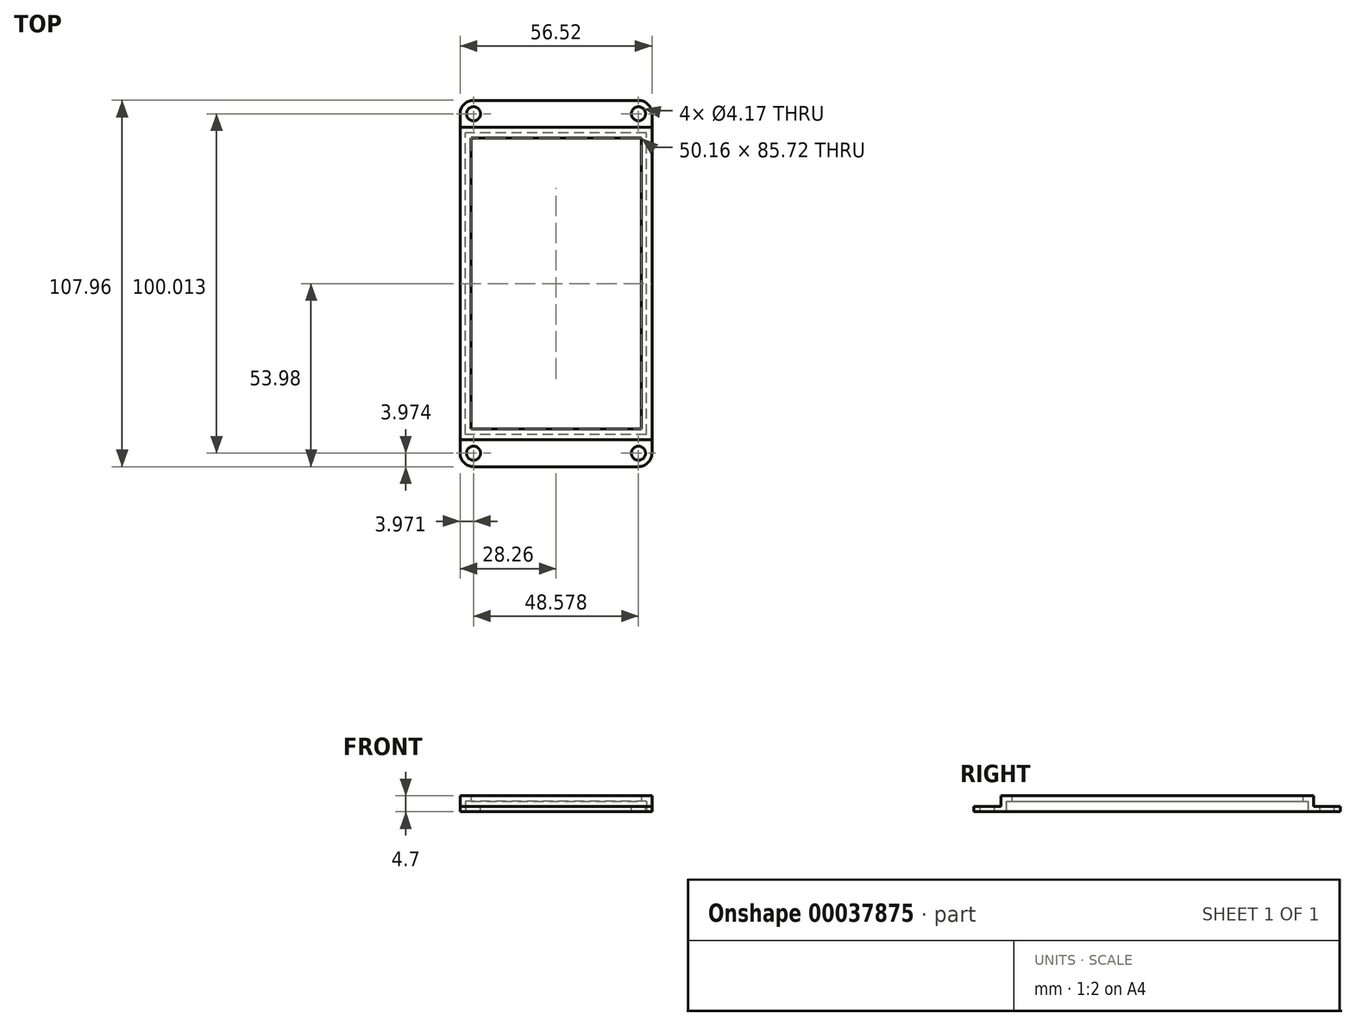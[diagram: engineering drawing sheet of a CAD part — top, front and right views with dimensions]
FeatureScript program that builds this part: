
annotation { "Feature Type Name" : "Feature", "Feature Type Description" : "" }
export const myFeature = defineFeature(function(context is Context, id is Id, definition is map)
    precondition{}
    {
        {
            var Q0;
            Q0=qCreatedBy(makeId("Top.planeOp"),FACE);
            var sketch = newSketch(context, id + "F0", { "sketchPlane" : qUnion([Q0])});
            skLineSegment(sketch, "E0.rect.bottom", {"start": v(26.67, -44.45) * mm, "end": v(-26.67, -44.45) * mm});
            skLineSegment(sketch, "E0.rect.top", {"start": v(26.67, 44.45) * mm, "end": v(-26.67, 44.45) * mm});
            skLineSegment(sketch, "E0.rect.left", {"start": v(26.67, -44.45) * mm, "end": v(26.67, 44.45) * mm});
            skLineSegment(sketch, "E0.rect.right", {"start": v(-26.67, -44.45) * mm, "end": v(-26.67, 44.45) * mm});
            skPoint(sketch, "E0.rect.middle", {"position": v(0, 0) * mm});
            skLineSegment(sketch, "E1.rect.bottom", {"start": v(28.26, -46.04) * mm, "end": v(-28.26, -46.04) * mm});
            skLineSegment(sketch, "E1.rect.top", {"start": v(28.26, 46.04) * mm, "end": v(-28.26, 46.04) * mm});
            skLineSegment(sketch, "E1.rect.left", {"start": v(28.26, -46.04) * mm, "end": v(28.26, 46.04) * mm});
            skLineSegment(sketch, "E1.rect.right", {"start": v(-28.26, -46.04) * mm, "end": v(-28.26, 46.04) * mm});
            skLineSegment(sketch, "E2.bottom", {"start": v(26.67, -44.45) * mm, "end": v(28.26, -44.45) * mm, "construction": true});
            skLineSegment(sketch, "E2.left", {"start": v(26.67, -44.45) * mm, "end": v(26.67, -46.04) * mm, "construction": true});
            skSolve(sketch);
        }
        {
            var Q0;
            Q0 = qSketchRegion(id + "F0", true);
            extrude(context, id + "F1", {"entities" : qUnion([Q0]), "depth" : 1.52 * mm});
        }
        {
            var Q0;
            Q0=makeQuery(id+"F1.opExtrude","CAP_FACE",FACE,{"disambiguationData":[OSD([sQuery(id+"F0.wireOp",EDGE,"E0.rect.bottom"),sQuery(id+"F0.wireOp",EDGE,"E0.rect.top"),sQuery(id+"F0.wireOp",EDGE,"E0.rect.left"),sQuery(id+"F0.wireOp",EDGE,"E0.rect.right"),sQuery(id+"F0.wireOp",EDGE,"E1.rect.bottom"),sQuery(id+"F0.wireOp",EDGE,"E1.rect.top"),sQuery(id+"F0.wireOp",EDGE,"E1.rect.left"),sQuery(id+"F0.wireOp",EDGE,"E1.rect.right")])],"isStart":true});
            var sketch = newSketch(context, id + "F2", { "sketchPlane" : qUnion([Q0])});
            skLineSegment(sketch, "E3", {"start": v(-26.67, 0) * mm, "end": v(26.67, 0) * mm, "construction": true});
            skPoint(sketch, "E3.endSnap0", {"position": v(-26.67, 0) * mm});
            skLineSegment(sketch, "E4.rect.bottom", {"start": v(-28.26, 53.98) * mm, "end": v(28.26, 53.98) * mm});
            skLineSegment(sketch, "E4.rect.top", {"start": v(-28.26, -53.97) * mm, "end": v(28.26, -53.97) * mm});
            skLineSegment(sketch, "E4.rect.left", {"start": v(-28.26, 53.98) * mm, "end": v(-28.26, -53.98) * mm});
            skLineSegment(sketch, "E4.rect.right", {"start": v(28.26, 53.98) * mm, "end": v(28.26, -53.98) * mm});
            skPoint(sketch, "E4.rect.middle", {"position": v(0, 0) * mm});
            skLineSegment(sketch, "E5", {"start": v(0, 53.98) * mm, "end": v(0, 50) * mm, "construction": true});
            skLineSegment(sketch, "E6", {"start": v(0, 50) * mm, "end": v(0, 46.04) * mm, "construction": true});
            skLineSegment(sketch, "E7", {"start": v(-24.29, 50) * mm, "end": v(24.29, 50) * mm, "construction": true});
            skLineSegment(sketch, "E8", {"start": v(24.29, 50) * mm, "end": v(28.26, 50) * mm, "construction": true});
            skLineSegment(sketch, "E9", {"start": v(0, -53.97) * mm, "end": v(0, -50) * mm, "construction": true});
            skLineSegment(sketch, "E10", {"start": v(-24.29, -50) * mm, "end": v(24.29, -50) * mm, "construction": true});
            skLineSegment(sketch, "E11.rect.bottom", {"start": v(-26.67, 44.45) * mm, "end": v(26.67, 44.45) * mm});
            skLineSegment(sketch, "E11.rect.top", {"start": v(-26.67, -44.45) * mm, "end": v(26.67, -44.45) * mm});
            skLineSegment(sketch, "E11.rect.left", {"start": v(-26.67, 44.45) * mm, "end": v(-26.67, -44.45) * mm});
            skLineSegment(sketch, "E11.rect.right", {"start": v(26.67, 44.45) * mm, "end": v(26.67, -44.45) * mm});
            skCircle(sketch, "E12", {"center": v(-24.29, 50) * mm, "radius": 2.08 * mm});
            skCircle(sketch, "E13", {"center": v(24.29, 50) * mm, "radius": 2.08 * mm});
            skCircle(sketch, "E14", {"center": v(24.29, -50) * mm, "radius": 2.08 * mm});
            skCircle(sketch, "E15", {"center": v(-24.29, -50) * mm, "radius": 2.08 * mm});
            skSolve(sketch);
        }
        {
            var Q0;
            Q0 = qSketchRegion(id + "F2", true);
            extrude(context, id + "F3", {"entities" : qUnion([Q0]), "operationType" : NewBodyOperationType.ADD, "depth" : 1.59 * mm});
        }
        {
            var Q0;
            Q0=makeQuery(id+"F1.opExtrude","CAP_FACE",FACE,{"disambiguationData":[OSD([sQuery(id+"F0.wireOp",EDGE,"E0.rect.bottom"),sQuery(id+"F0.wireOp",EDGE,"E0.rect.top"),sQuery(id+"F0.wireOp",EDGE,"E0.rect.left"),sQuery(id+"F0.wireOp",EDGE,"E0.rect.right"),sQuery(id+"F0.wireOp",EDGE,"E1.rect.bottom"),sQuery(id+"F0.wireOp",EDGE,"E1.rect.top"),sQuery(id+"F0.wireOp",EDGE,"E1.rect.left"),sQuery(id+"F0.wireOp",EDGE,"E1.rect.right")])],"isStart":false});
            var sketch = newSketch(context, id + "F4", { "sketchPlane" : qUnion([Q0])});
            skLineSegment(sketch, "E16", {"start": v(-26.67, 0) * mm, "end": v(26.67, 0) * mm, "construction": true});
            skLineSegment(sketch, "E17.rect.bottom", {"start": v(-28.26, -46.04) * mm, "end": v(28.26, -46.04) * mm});
            skLineSegment(sketch, "E17.rect.top", {"start": v(-28.26, 46.04) * mm, "end": v(28.26, 46.04) * mm});
            skLineSegment(sketch, "E17.rect.left", {"start": v(-28.26, -46.04) * mm, "end": v(-28.26, 46.04) * mm});
            skLineSegment(sketch, "E17.rect.right", {"start": v(28.26, -46.04) * mm, "end": v(28.26, 46.04) * mm});
            skPoint(sketch, "E17.rect.middle", {"position": v(0, 0) * mm});
            skLineSegment(sketch, "E18.rect.bottom", {"start": v(-25.08, -42.86) * mm, "end": v(25.08, -42.86) * mm});
            skLineSegment(sketch, "E18.rect.top", {"start": v(-25.08, 42.86) * mm, "end": v(25.08, 42.86) * mm});
            skLineSegment(sketch, "E18.rect.left", {"start": v(-25.08, -42.86) * mm, "end": v(-25.08, 42.86) * mm});
            skLineSegment(sketch, "E18.rect.right", {"start": v(25.08, -42.86) * mm, "end": v(25.08, 42.86) * mm});
            skSolve(sketch);
        }
        {
            var Q0;
            Q0 = qSketchRegion(id + "F4", true);
            extrude(context, id + "F5", {"entities" : qUnion([Q0]), "operationType" : NewBodyOperationType.ADD, "depth" : 1.59 * mm});
        }
        {
            var Q0;
            Q0=makeQuery(id+"F3.opExtrude","SWEPT_EDGE",EDGE,{"disambiguationData":[OSD([sQuery(id+"F2.wireOp",EDGE,"E4.rect.bottom"),sQuery(id+"F2.wireOp",EDGE,"E4.rect.left")])]});
            var Q1;
            Q1=makeQuery(id+"F3.opExtrude","SWEPT_EDGE",EDGE,{"disambiguationData":[OSD([sQuery(id+"F2.wireOp",EDGE,"E4.rect.bottom"),sQuery(id+"F2.wireOp",EDGE,"E4.rect.right")])]});
            var Q2;
            Q2=makeQuery(id+"F3.opExtrude","SWEPT_EDGE",EDGE,{"disambiguationData":[OSD([sQuery(id+"F2.wireOp",EDGE,"E4.rect.top"),sQuery(id+"F2.wireOp",EDGE,"E4.rect.right")])]});
            var Q3;
            Q3=makeQuery(id+"F3.opExtrude","SWEPT_EDGE",EDGE,{"disambiguationData":[OSD([sQuery(id+"F2.wireOp",EDGE,"E4.rect.top"),sQuery(id+"F2.wireOp",EDGE,"E4.rect.left")])]});
            fillet(context, id + "F6", {"entities" : qUnion([Q0, Q1, Q2, Q3]), "radius" : 3.97 * mm, "tangentPropagation" : true, "allowEdgeOverflow" : false});
        }
    });
